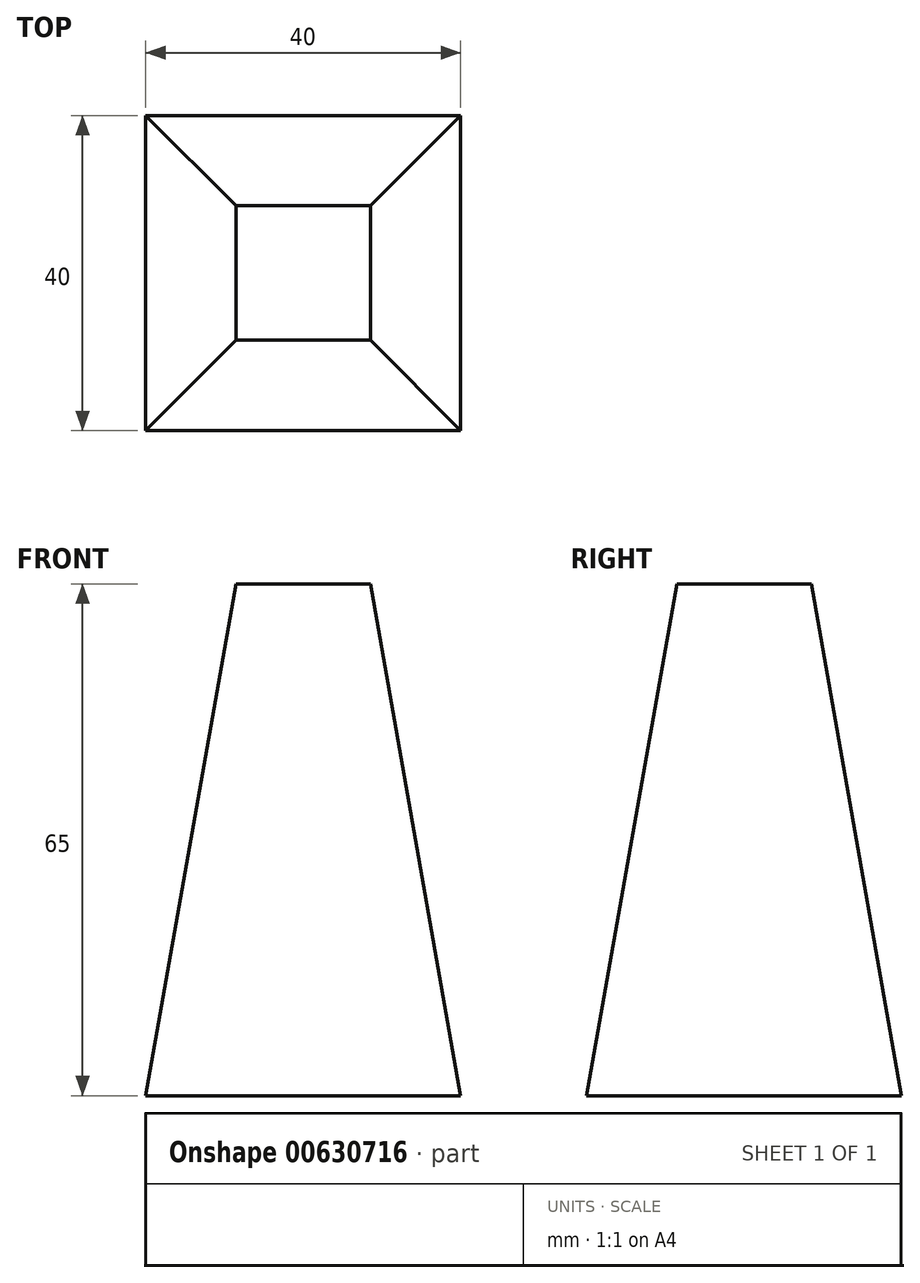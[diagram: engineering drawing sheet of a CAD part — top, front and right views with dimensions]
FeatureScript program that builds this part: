
annotation { "Feature Type Name" : "Feature", "Feature Type Description" : "" }
export const myFeature = defineFeature(function(context is Context, id is Id, definition is map)
    precondition{}
    {
        {
            var Q0;
            Q0=qCreatedBy(makeId("Top.planeOp"),FACE);
            var sketch = newSketch(context, id + "F0", { "sketchPlane" : qUnion([Q0])});
            skLineSegment(sketch, "E0.bottom", {"start": v(0, 0) * mm, "end": v(40, 0) * mm});
            skLineSegment(sketch, "E0.top", {"start": v(0, -40) * mm, "end": v(40, -40) * mm});
            skLineSegment(sketch, "E0.left", {"start": v(0, 0) * mm, "end": v(0, -40) * mm});
            skLineSegment(sketch, "E0.right", {"start": v(40, 0) * mm, "end": v(40, -40) * mm});
            skSolve(sketch);
        }
        {
            var Q0;
            Q0 = qSketchRegion(id + "F0", true);
            extrude(context, id + "F1", {"entities" : qUnion([Q0]), "depth" : 65 * mm, "offsetDistance" : 25 * mm, "hasDraft" : true, "draftAngle" : 10 * degree, "draftPullDirection" : true});
        }
    });
